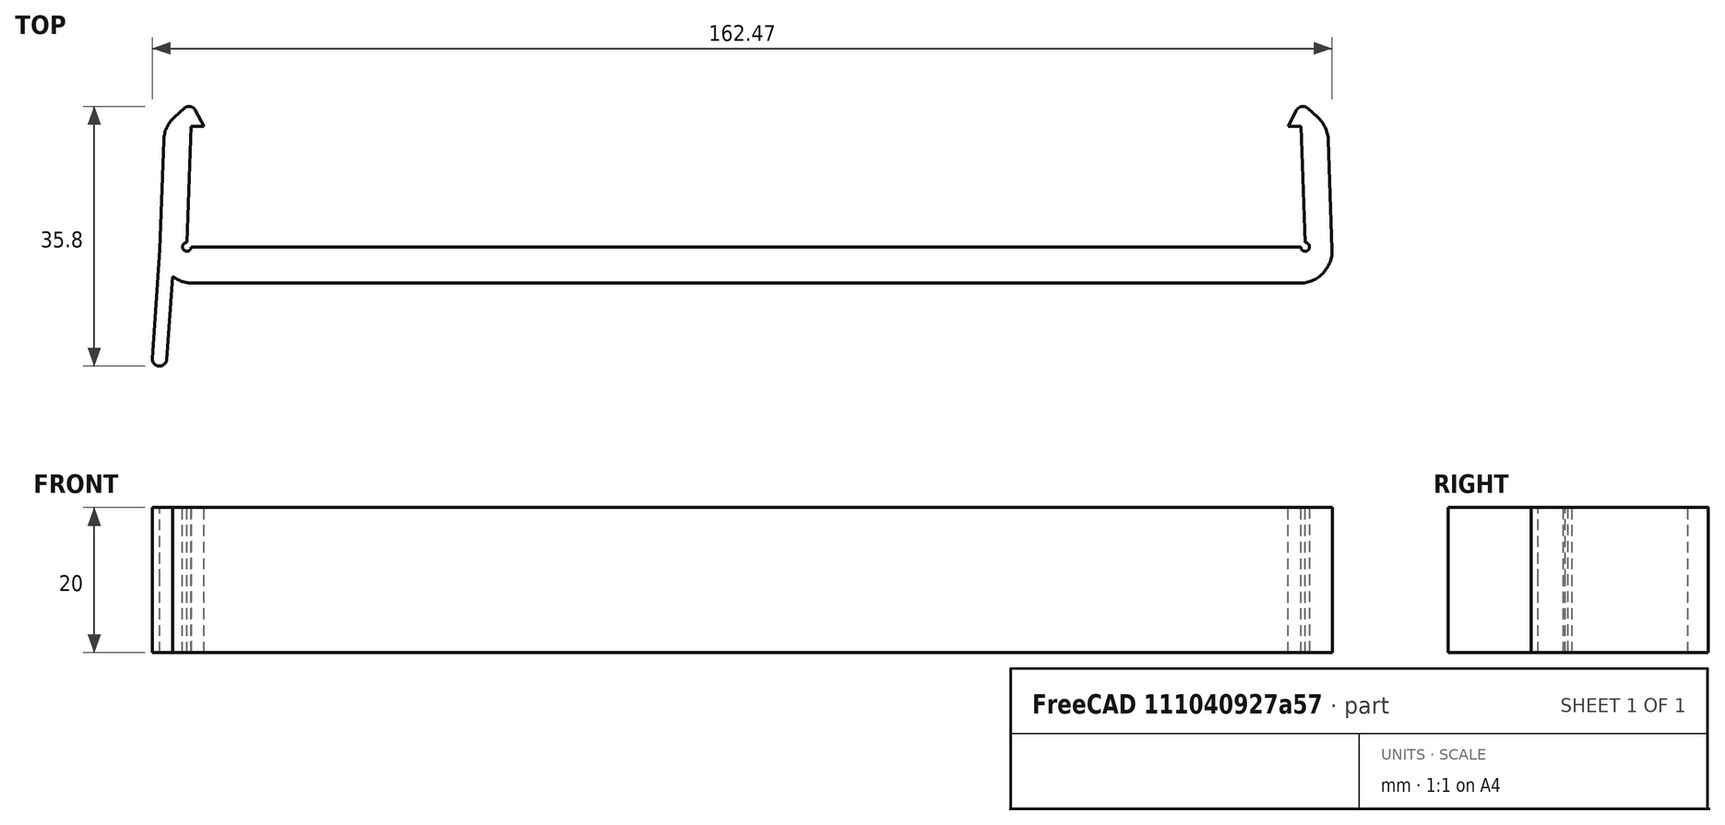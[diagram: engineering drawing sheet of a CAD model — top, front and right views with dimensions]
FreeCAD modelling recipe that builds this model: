
FCSTD DOCUMENT  (FreeCAD 0.21R33771 (Git))
Label: clamp
License: All rights reserved
LicenseURL: https://en.wikipedia.org/wiki/All_rights_reserved
objects: Sketcher::SketchObject×3, PartDesign::Pad×3, PartDesign::Fillet×2, PartDesign::Pocket×1, PartDesign::Body×1, Mesh::Feature×1
note: 16 computed .brp shape members not serialized (recipe doc carries the construction recipe); baked Part::Feature solids carry a one-line shape summary decoded from their .brp

FEATURE [Sketcher::SketchObject] Sketch
  FullyConstrained = true
  MapMode = 5
  sketch-geometry (18):
    g0: LineSegment StartX=0 StartY=0 StartZ=0 EndX=80.8746 EndY=0 EndZ=0
    g1: LineSegment StartX=80.8746 StartY=0 StartZ=0 EndX=80.1207 EndY=21.5899 EndZ=0
    g2: LineSegment StartX=76.4207 StartY=21.5899 StartZ=0 EndX=77 EndY=5 EndZ=0
    g3: LineSegment StartX=77 StartY=5 StartZ=0 EndX=-77 EndY=5 EndZ=0
    g4: LineSegment StartX=-80.8746 StartY=0 StartZ=0 EndX=0 EndY=0 EndZ=0
    g5: LineSegment StartX=-76.4207 StartY=24.9752 StartZ=0 EndX=-74.6207 EndY=21.5899 EndZ=0
    g6: LineSegment StartX=-74.6207 StartY=21.5899 StartZ=0 EndX=-76.4207 EndY=21.5899 EndZ=0
    g7: LineSegment StartX=-76.4207 StartY=21.5899 StartZ=0 EndX=-77 EndY=5 EndZ=0
    g8: LineSegment StartX=-76.4207 StartY=21.5899 StartZ=0 EndX=-76.4207 EndY=24.9752 EndZ=0
    g9: LineSegment StartX=-80.1207 StartY=21.5899 StartZ=0 EndX=-76.4207 EndY=24.9752 EndZ=0
    g10: LineSegment StartX=-80.1207 StartY=21.5899 StartZ=0 EndX=-76.4207 EndY=21.5899 EndZ=0
    g11: LineSegment StartX=76.4207 StartY=21.5899 StartZ=0 EndX=80.1207 EndY=21.5899 EndZ=0
    g12: LineSegment StartX=80.1207 StartY=21.5899 StartZ=0 EndX=76.4207 EndY=24.9752 EndZ=0
    g13: LineSegment StartX=76.4207 StartY=24.9752 StartZ=0 EndX=74.6207 EndY=21.5899 EndZ=0
    g14: LineSegment StartX=74.6207 StartY=21.5899 StartZ=0 EndX=76.4207 EndY=21.5899 EndZ=0
    g15: LineSegment StartX=76.4207 StartY=21.5899 StartZ=0 EndX=76.4207 EndY=24.9752 EndZ=0
    g16: LineSegment StartX=-76.4207 StartY=24.9752 StartZ=0 EndX=76.4207 EndY=24.9752 EndZ=0
    g17: LineSegment StartX=-80.1207 StartY=21.5899 StartZ=0 EndX=-80.8746 EndY=0 EndZ=0
  constraints (46):
    c: Coincident(g0,g-1)
    c: PointOnObject(g0,g-1)
    c: Coincident(g1,g0)
    c: Coincident(g4,g0)
    c: Coincident(g3,g2)
    c: Symmetric(g3,g2,g-2)
    c: Distance(g2,g0) = 5
    c: Coincident(g6,g5)
    c: Horizontal(g6)
    c: Coincident(g7,g3)
    c: Coincident(g6,g7)
    c: Coincident(g8,g6)
    c: Vertical(g8)
    c: Distance(g6,g5) = 1.8
    c: Coincident(g5,g8)
    c: Distance(g6,g3) = 16.6
    c: Coincident(g9,g5)
    c: Coincident(g10,g6)
    c: Horizontal(g10)
    c: Angle(g7,g5) = 0.523599
    c: DistanceX(g3,g3) = 154
    c: Coincident(g11,g2)
    c: Coincident(g11,g1)
    c: Horizontal(g11)
    c: Coincident(g12,g1)
    c: Coincident(g13,g12)
    c: Coincident(g14,g13)
    c: Coincident(g14,g2)
    c: Horizontal(g14)
    c: Equal(g14,g6)
    c: Coincident(g15,g2)
    c: Coincident(g15,g12)
    c: Vertical(g15)
    c: Coincident(g16,g5)
    c: Coincident(g16,g12)
    c: Horizontal(g16)
    c: Equal(g11,g10)
    c: Distance(g5,g9) = 5.5
    c: Symmetric(g6,g2,g-2)
    c: Angle(g7,g-2) = 0.0349066
    c: Horizontal(g4)
    c: Coincident(g17,g9)
    c: Coincident(g17,g4)
    c: Coincident(g9,g10)
    c: Parallel(g17,g7)
    c: Parallel(g2,g1)
FEATURE [PartDesign::Pad] Pad  label="clamp body"
  Direction = (0,0,1)
  Length = 20
  Length2 = 10
  Midplane = true
  Profile = -> Sketch
  ReferenceAxis = -> Sketch [N_Axis]
  Type = 0
FEATURE [Sketcher::SketchObject] Sketch001
  ExternalGeometry = -> [Pad]
  FullyConstrained = true
  MapMode = 2
  Support = -> [XY_Plane]
  sketch-geometry (2):
    g0: Circle CenterX=-77 CenterY=5 CenterZ=0 NormalX=0 NormalY=0 NormalZ=1 AngleXU=0 Radius=0.6
    g1: Circle CenterX=77 CenterY=5 CenterZ=0 NormalX=0 NormalY=0 NormalZ=1 AngleXU=0 Radius=0.6
  constraints (4):
    c: Coincident(g0,g-3)
    c: Coincident(g1,g-3)
    c: Equal(g1,g0)
    c: Radius(g0) = 0.6
FEATURE [PartDesign::Pocket] Pocket  label="inner rounding"
  BaseFeature = -> Pad
  Direction = (0,0,-1)
  Length = 5
  Length2 = 5
  Midplane = true
  Profile = -> Sketch001
  ReferenceAxis = -> Sketch001 [N_Axis]
  Type = 1
FEATURE [PartDesign::Fillet] Fillet  label="outer rounding"
  Base = -> Pocket [Edge2,Edge38,Edge1,Edge48]
  BaseFeature = -> Pocket
  Radius = 4.5
  SupportTransform = false
  UseAllEdges = false
FEATURE [Sketcher::SketchObject] Sketch002
  ExternalGeometry = -> [Fillet]
  FullyConstrained = true
  MapMode = 5
  Support = -> [XY_Plane]
  expr: Constraints[6] = 180 - 2
  sketch-geometry (4):
    g0: LineSegment StartX=-80.712 StartY=4.65705 StartZ=0 EndX=-81.7621 EndY=-10.3604 EndZ=0
    g1: LineSegment StartX=-79.767 StartY=-10.5 StartZ=0 EndX=-78.7168 EndY=4.51753 EndZ=0
    g2: LineSegment StartX=-78.7168 StartY=4.51753 StartZ=0 EndX=-80.712 EndY=4.65705 EndZ=0
    g3: ArcOfCircle CenterX=-80.7645 CenterY=-10.4302 CenterZ=0 NormalX=0 NormalY=0 NormalZ=1 AngleXU=0 Radius=1 StartAngle=3.07178 EndAngle=6.21337
  constraints (10):
    c: Coincident(g0,g-3)
    c: Coincident(g2,g1)
    c: Coincident(g2,g0)
    c: Parallel(g0,g1)
    c: Angle(g0,g2) = 1.5708
    c: Equal(g0,g-3)
    c: Angle(g-3,g0) = 3.10669
    c: Distance(g0,g1) = 2
    c: Tangent(g3,g0) = -1.5708
    c: Tangent(g3,g1) = -1.5708
FEATURE [PartDesign::Pad] Pad001  label="lever 1"
  BaseFeature = -> Fillet
  Direction = (0,0,1)
  Length = 10
  Length2 = 10
  Profile = -> Sketch002
  ReferenceAxis = -> Sketch002 [N_Axis]
  Type = 3
  UpToFace = -> Fillet [Face5]
FEATURE [PartDesign::Pad] Pad002  label="lever 2"
  BaseFeature = -> Pad001
  Direction = (0,0,1)
  Length = 10
  Length2 = 10
  Profile = -> Sketch002
  ReferenceAxis = -> Sketch002 [N_Axis]
  Type = 3
  UpToFace = -> Pad001 [Face2]
FEATURE [PartDesign::Fillet] Fillet001  label="peak roundings"
  Base = -> Pad002 [Edge54,Edge64]
  BaseFeature = -> Pad002
  Radius = 1
  SupportTransform = false
  UseAllEdges = false
FEATURE [PartDesign::Body] Body
  Group = -> [Sketch,Pad,Sketch001,Pocket,Fillet,Sketch002,Pad001,Pad002,Fillet001]
  Origin = -> Origin
  Tip = -> Fillet001
FEATURE [Mesh::Feature] Mesh  label="print-clamp"
